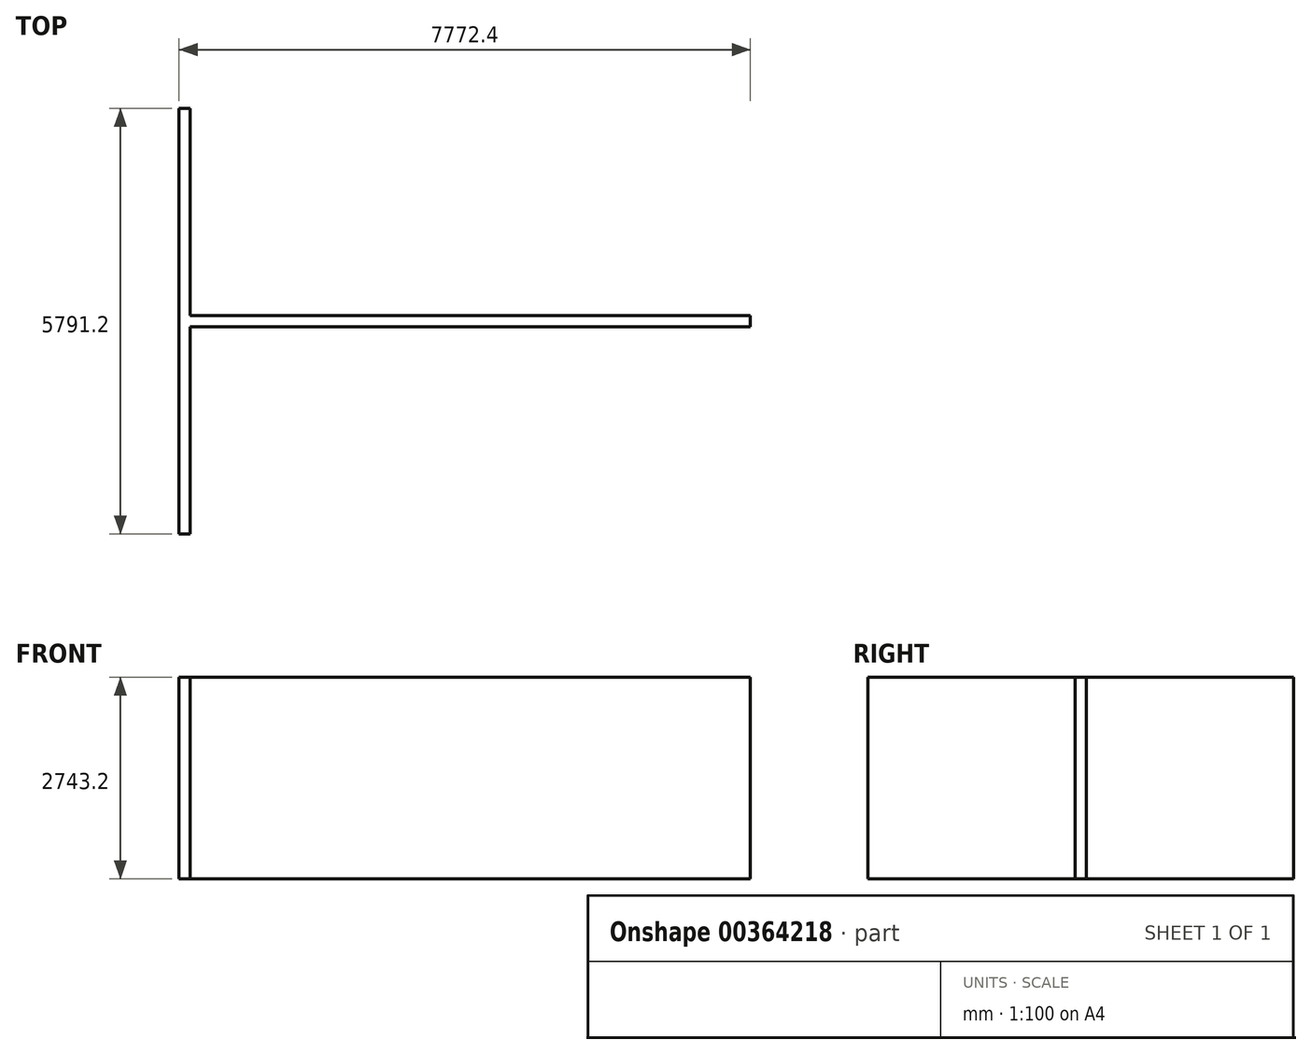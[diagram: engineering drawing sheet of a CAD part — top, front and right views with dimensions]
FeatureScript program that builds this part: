
annotation { "Feature Type Name" : "Feature", "Feature Type Description" : "" }
export const myFeature = defineFeature(function(context is Context, id is Id, definition is map)
    precondition{}
    {
        {
            var Q0;
            Q0=qCreatedBy(makeId("Top.planeOp"),FACE);
            var sketch = newSketch(context, id + "F0", { "sketchPlane" : qUnion([Q0])});
            skLineSegment(sketch, "E0.bottom", {"start": v(0, 0) * mm, "end": v(152.4, 0) * mm});
            skLineSegment(sketch, "E0.top", {"start": v(0, 5791.2) * mm, "end": v(152.4, 5791.2) * mm});
            skLineSegment(sketch, "E0.left", {"start": v(0, 0) * mm, "end": v(0, 5791.2) * mm});
            skLineSegment(sketch, "E0.right", {"start": v(152.4, 0) * mm, "end": v(152.4, 2819.4) * mm});
            skLineSegment(sketch, "E1.bottom", {"start": v(152.4, 2971.8) * mm, "end": v(7772.4, 2971.8) * mm});
            skLineSegment(sketch, "E1.top", {"start": v(152.4, 2819.4) * mm, "end": v(7772.4, 2819.4) * mm});
            skLineSegment(sketch, "E1.right", {"start": v(7772.4, 2971.8) * mm, "end": v(7772.4, 2819.4) * mm});
            skLineSegment(sketch, "E2.trimOffspring", {"start": v(152.4, 2971.8) * mm, "end": v(152.4, 5791.2) * mm});
            skSolve(sketch);
        }
        {
            var Q0;
            Q0 = qSketchRegion(id + "F0", true);
            extrude(context, id + "F1", {"entities" : qUnion([Q0]), "depth" : 2743.2 * mm});
        }
    });
